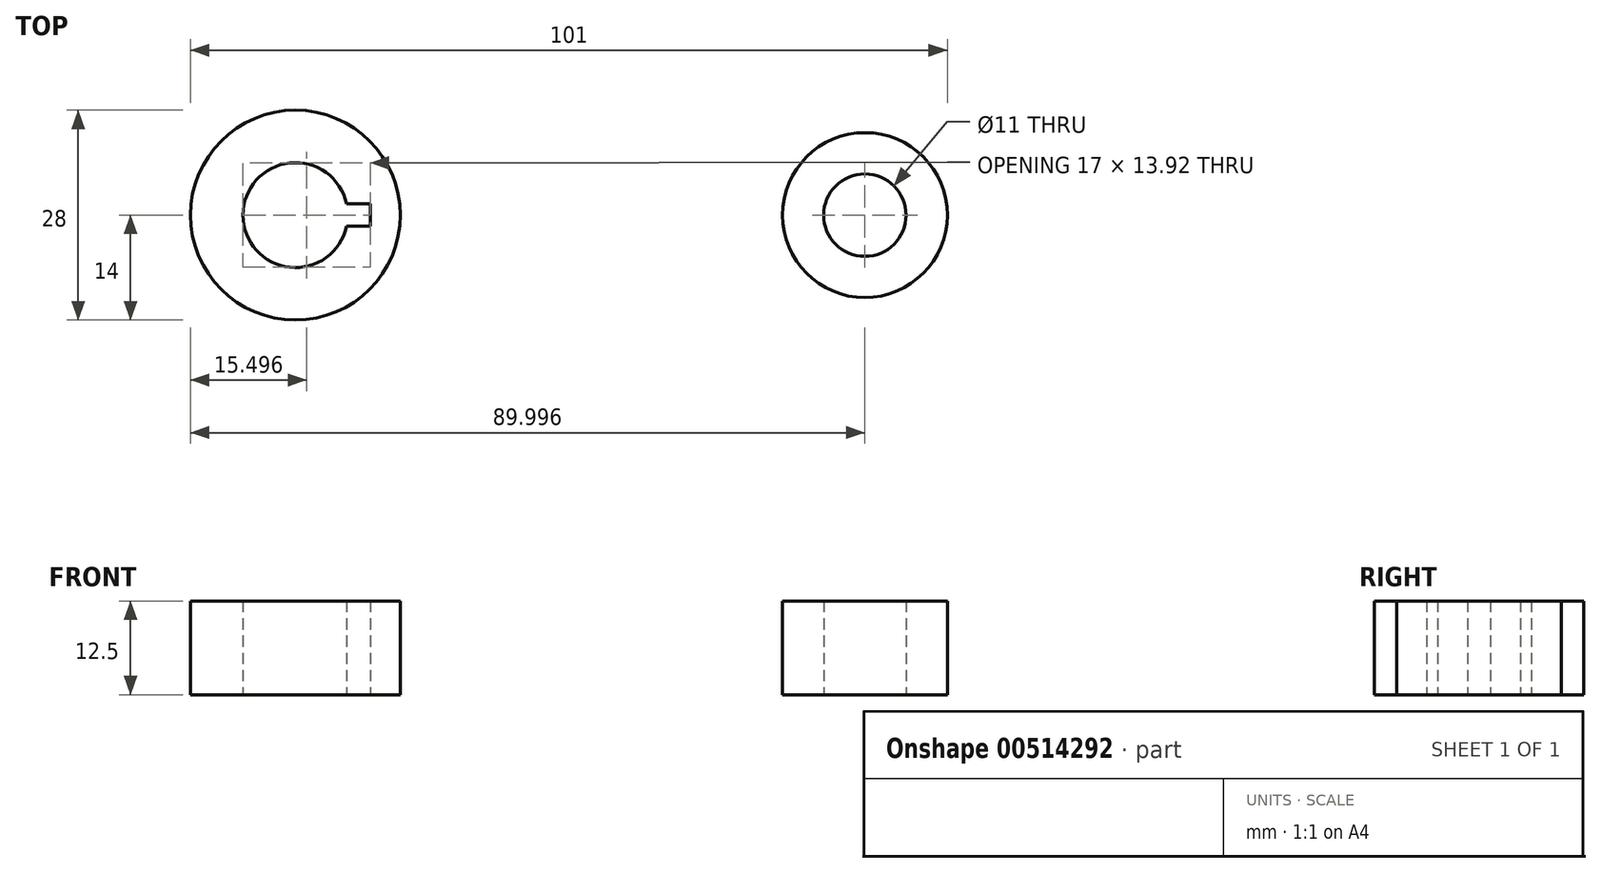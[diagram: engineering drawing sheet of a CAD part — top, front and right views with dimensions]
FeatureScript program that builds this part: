
annotation { "Feature Type Name" : "Feature", "Feature Type Description" : "" }
export const myFeature = defineFeature(function(context is Context, id is Id, definition is map)
    precondition{}
    {
        {
            var Q0;
            Q0=qCreatedBy(makeId("Top.planeOp"),FACE);
            var sketch = newSketch(context, id + "F0", { "sketchPlane" : qUnion([Q0])});
            skArc(sketch, "E0", {"start": v(-46.35, 1.5) * mm, "mid": v(-60.18, 0) * mm, "end": v(-46.35, -1.5) * mm});
            skCircle(sketch, "E1", {"center": v(-53.18, 0) * mm, "radius": 14 * mm});
            skLineSegment(sketch, "E2", {"start": v(-46.35, 1.5) * mm, "end": v(-43.18, 1.5) * mm});
            skLineSegment(sketch, "E3", {"start": v(-43.18, 1.5) * mm, "end": v(-43.18, -1.5) * mm});
            skLineSegment(sketch, "E4", {"start": v(-43.18, -1.5) * mm, "end": v(-46.35, -1.5) * mm});
            skCircle(sketch, "E5", {"center": v(22.82, 0) * mm, "radius": 5.5 * mm});
            skCircle(sketch, "E6", {"center": v(22.82, 0) * mm, "radius": 11 * mm});
            skSolve(sketch);
        }
        {
            var Q0;
            Q0=makeQuery(id+"F0.imprint","IMPRINT",FACE,{"disambiguationData":[TD([[makeQuery(id+"F0.imprint","IMPRINT",EDGE,{"derivedFrom":sQuery(id+"F0.wireOp",EDGE,"E0")}),-1.0]])]});
            var Q1;
            Q1=makeQuery(id+"F0.imprint","IMPRINT",FACE,{"disambiguationData":[TD([[makeQuery(id+"F0.imprint","IMPRINT",EDGE,{"derivedFrom":sQuery(id+"F0.wireOp",EDGE,"E5")}),-1.0]])]});
            extrude(context, id + "F1", {"entities" : qUnion([Q0, Q1]), "depth" : 12.5 * mm});
        }
        {
            var Q0;
            Q0=qCreatedBy(makeId("Top.planeOp"),FACE);
            cPlane(context, id + "F2", {"entities" : qUnion([Q0]), "cplaneType" : CPlaneType.OFFSET, "offset" : 3.25 * mm, "width" : 150 * mm, "height" : 150 * mm});
        }
    });
